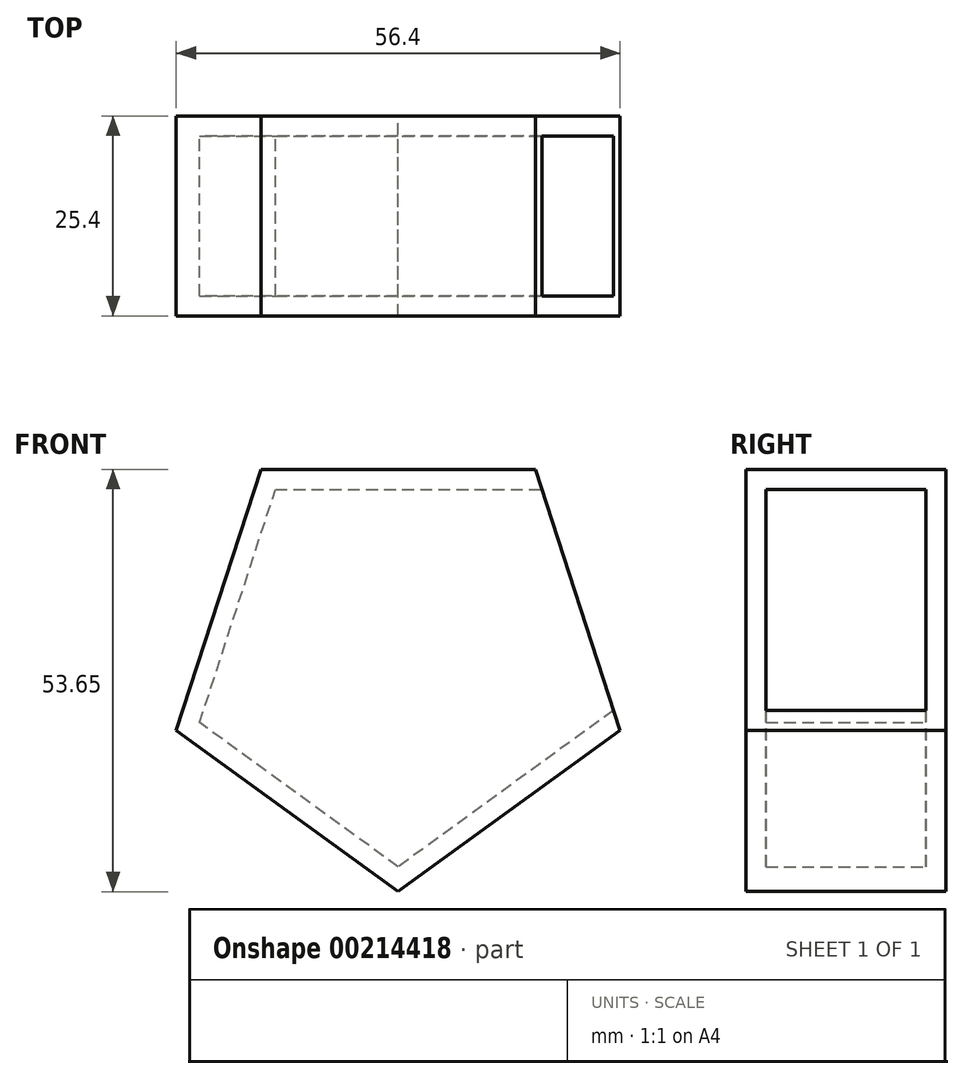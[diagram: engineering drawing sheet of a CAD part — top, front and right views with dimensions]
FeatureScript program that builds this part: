
annotation { "Feature Type Name" : "Feature", "Feature Type Description" : "" }
export const myFeature = defineFeature(function(context is Context, id is Id, definition is map)
    precondition{}
    {
        {
            var Q0;
            Q0=qCreatedBy(makeId("Front.planeOp"),FACE);
            var sketch = newSketch(context, id + "F0", { "sketchPlane" : qUnion([Q0])});
            skCircle(sketch, "E0.cCircle", {"center": v(0, 0) * mm, "radius": 24 * mm, "construction": true});
            skLineSegment(sketch, "E0.0", {"start": v(-17.43, 24) * mm, "end": v(17.43, 24) * mm});
            skLineSegment(sketch, "E0.1", {"start": v(17.43, 24) * mm, "end": v(28.2, -9.16) * mm});
            skLineSegment(sketch, "E0.2", {"start": v(28.2, -9.16) * mm, "end": v(0, -29.66) * mm});
            skLineSegment(sketch, "E0.3", {"start": v(0, -29.66) * mm, "end": v(-28.2, -9.16) * mm});
            skLineSegment(sketch, "E0.4", {"start": v(-28.2, -9.16) * mm, "end": v(-17.43, 24) * mm});
            skPoint(sketch, "E0.0.midPoint", {"position": v(0, 24) * mm});
            skSolve(sketch);
        }
        {
            var Q0;
            Q0=makeQuery(id+"F0.imprint","IMPRINT",FACE,{"disambiguationData":[TD([[makeQuery(id+"F0.imprint","IMPRINT",EDGE,{"derivedFrom":sQuery(id+"F0.wireOp",EDGE,"E0.0")}),-1.0]])]});
            extrude(context, id + "F1", {"entities" : qUnion([Q0]), "depth" : 25.4 * mm});
        }
        {
            var Q0;
            Q0=makeQuery(id+"F1.opExtrude","SWEPT_FACE",FACE,{"disambiguationData":[OSD([sQuery(id+"F0.wireOp",EDGE,"E0.1")])]});
            shell(context, id + "F2", {"entities" : qUnion([Q0]), "thickness" : 2.54 * mm});
        }
    });
